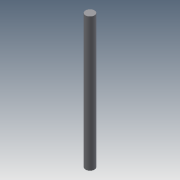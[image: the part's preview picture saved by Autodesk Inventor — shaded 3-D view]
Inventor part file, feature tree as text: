
AUTODESK INVENTOR PART (.ipt)
format: ipt  version: 2013 (Build 170138000, 138)  size: 61,952 bytes
history: native  units: mm
features: extrude x1, sketch x1
ambient origin geometry x8: Origin, YZ Plane, XZ Plane, XY Plane, X Axis, Y Axis, Z Axis, Center Point
bodies: Solid1 (feature_tree)
feature tree (2):
  extrude  "Extrusion1"  Depth=90.0mm TaperAngle=0.0deg
  sketch  "Sketch1"  dims[d0=6.0mm d1=90.0mm d2=0.0mm]
